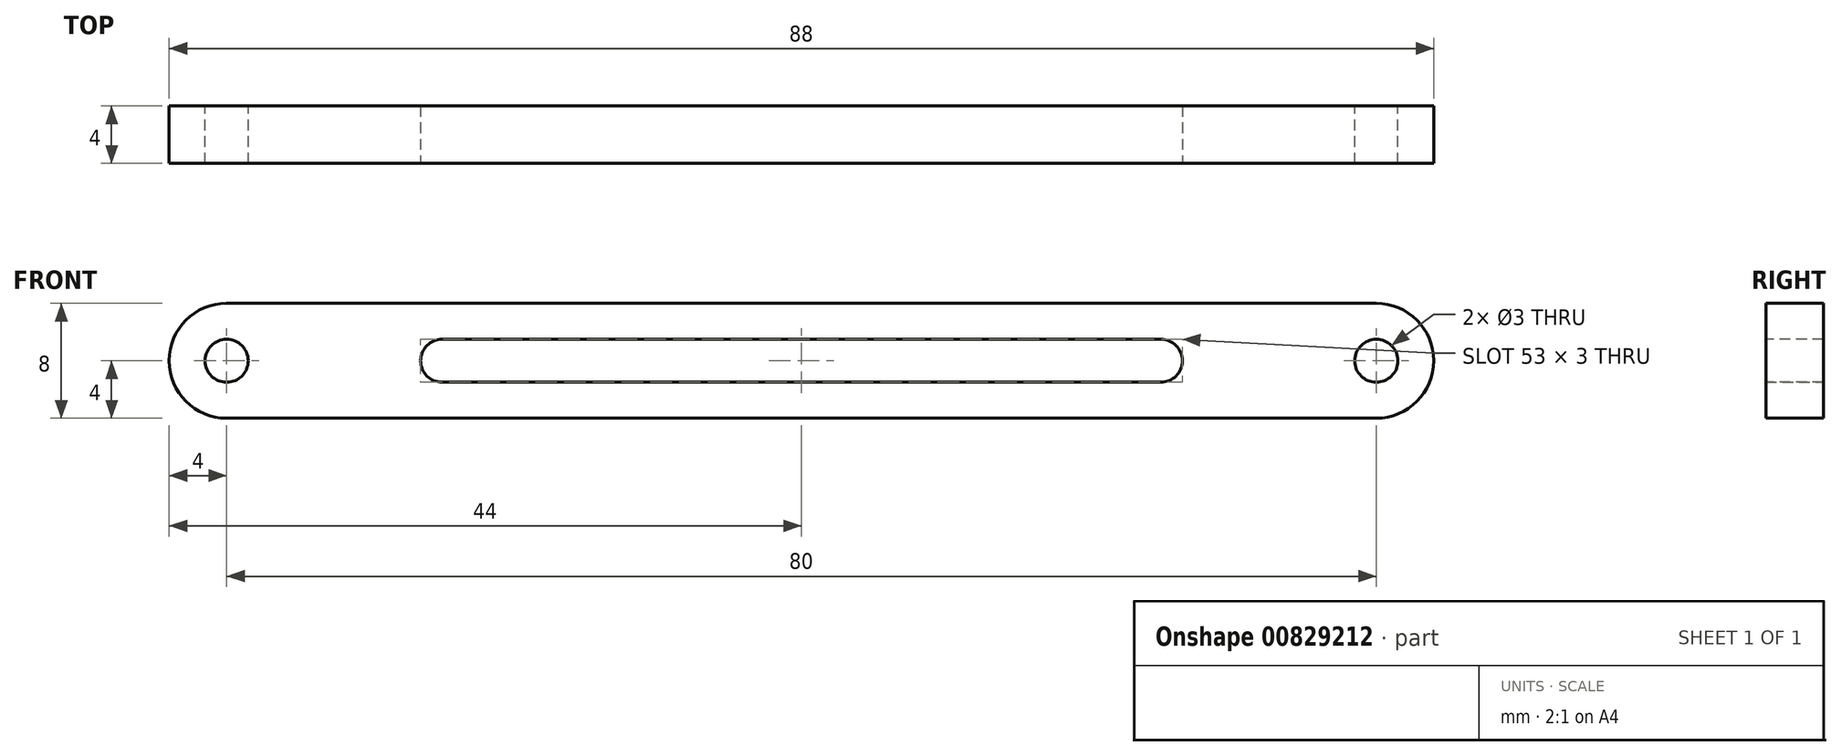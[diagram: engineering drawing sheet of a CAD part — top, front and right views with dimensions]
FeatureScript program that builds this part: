
annotation { "Feature Type Name" : "Feature", "Feature Type Description" : "" }
export const myFeature = defineFeature(function(context is Context, id is Id, definition is map)
    precondition{}
    {
        {
            var Q0;
            Q0=qCreatedBy(makeId("Front.planeOp"),FACE);
            var sketch = newSketch(context, id + "F0", { "sketchPlane" : qUnion([Q0])});
            skLineSegment(sketch, "E0.bottom", {"start": v(40, 4) * mm, "end": v(-40, 4) * mm});
            skLineSegment(sketch, "E0.top", {"start": v(40, -4) * mm, "end": v(-40, -4) * mm});
            skPoint(sketch, "E0.middle", {"position": v(0, 0) * mm});
            skArc(sketch, "E1", {"start": v(40, -4) * mm, "mid": v(44, 0) * mm, "end": v(40, 4) * mm});
            skArc(sketch, "E2", {"start": v(-40, 4) * mm, "mid": v(-44, 0) * mm, "end": v(-40, -4) * mm});
            skCircle(sketch, "E3", {"center": v(-40, 0) * mm, "radius": 1.5 * mm});
            skCircle(sketch, "E4", {"center": v(-10, 0) * mm, "radius": 1.5 * mm});
            skCircle(sketch, "E5", {"center": v(40, 0) * mm, "radius": 1.5 * mm});
            skSolve(sketch);
        }
        {
            var Q0;
            Q0=makeQuery(id+"F0.imprint","IMPRINT",FACE,{"disambiguationData":[TD([[makeQuery(id+"F0.imprint","IMPRINT",EDGE,{"derivedFrom":sQuery(id+"F0.wireOp",EDGE,"E0.bottom")}),1.0]])]});
            extrude(context, id + "F1", {"entities" : qUnion([Q0]), "endBound" : BoundingType.SYMMETRIC, "depth" : 4 * mm, "offsetDistance" : 25 * mm});
        }
        {
            var Q0;
            Q0=makeQuery(id+"F1.opExtrude","CAP_FACE",FACE,{"disambiguationData":[OSD([sQuery(id+"F0.wireOp",EDGE,"E0.bottom"),sQuery(id+"F0.wireOp",EDGE,"E0.top"),sQuery(id+"F0.wireOp",EDGE,"E1"),sQuery(id+"F0.wireOp",EDGE,"E2"),sQuery(id+"F0.wireOp",EDGE,"E3"),sQuery(id+"F0.wireOp",EDGE,"E4"),sQuery(id+"F0.wireOp",EDGE,"E5")])],"isStart":false});
            var sketch = newSketch(context, id + "F2", { "sketchPlane" : qUnion([Q0])});
            skLineSegment(sketch, "E6.bottom", {"start": v(-25, 1.5) * mm, "end": v(25, 1.5) * mm});
            skLineSegment(sketch, "E6.top", {"start": v(-25, -1.5) * mm, "end": v(25, -1.5) * mm});
            skPoint(sketch, "E6.middle", {"position": v(0, 0) * mm});
            skArc(sketch, "E7", {"start": v(-25, 1.5) * mm, "mid": v(-26.5, 0) * mm, "end": v(-25, -1.5) * mm});
            skArc(sketch, "E8", {"start": v(25, -1.5) * mm, "mid": v(26.5, 0) * mm, "end": v(25, 1.5) * mm});
            skSolve(sketch);
        }
        {
            var Q0;
            {var subQ0=sQuery(id+"F2.wireOp",EDGE,"E7");Q0=makeQuery(id+"F2.imprint","IMPRINT",FACE,{"disambiguationData":[TD([[makeQuery(id+"F2.imprint","IMPRINT",EDGE,{"derivedFrom":subQ0}),1.0]])]});}
            var Q1;
            {var subQ0=sQuery(id+"F2.wireOp",EDGE,"E8");Q1=makeQuery(id+"F2.imprint","IMPRINT",FACE,{"disambiguationData":[TD([[makeQuery(id+"F2.imprint","IMPRINT",EDGE,{"derivedFrom":subQ0}),1.0]])]});}
            extrude(context, id + "F3", {"entities" : qUnion([Q0, Q1]), "operationType" : NewBodyOperationType.REMOVE, "oppositeDirection" : true, "depth" : 25 * mm, "offsetDistance" : 25 * mm});
        }
    });
